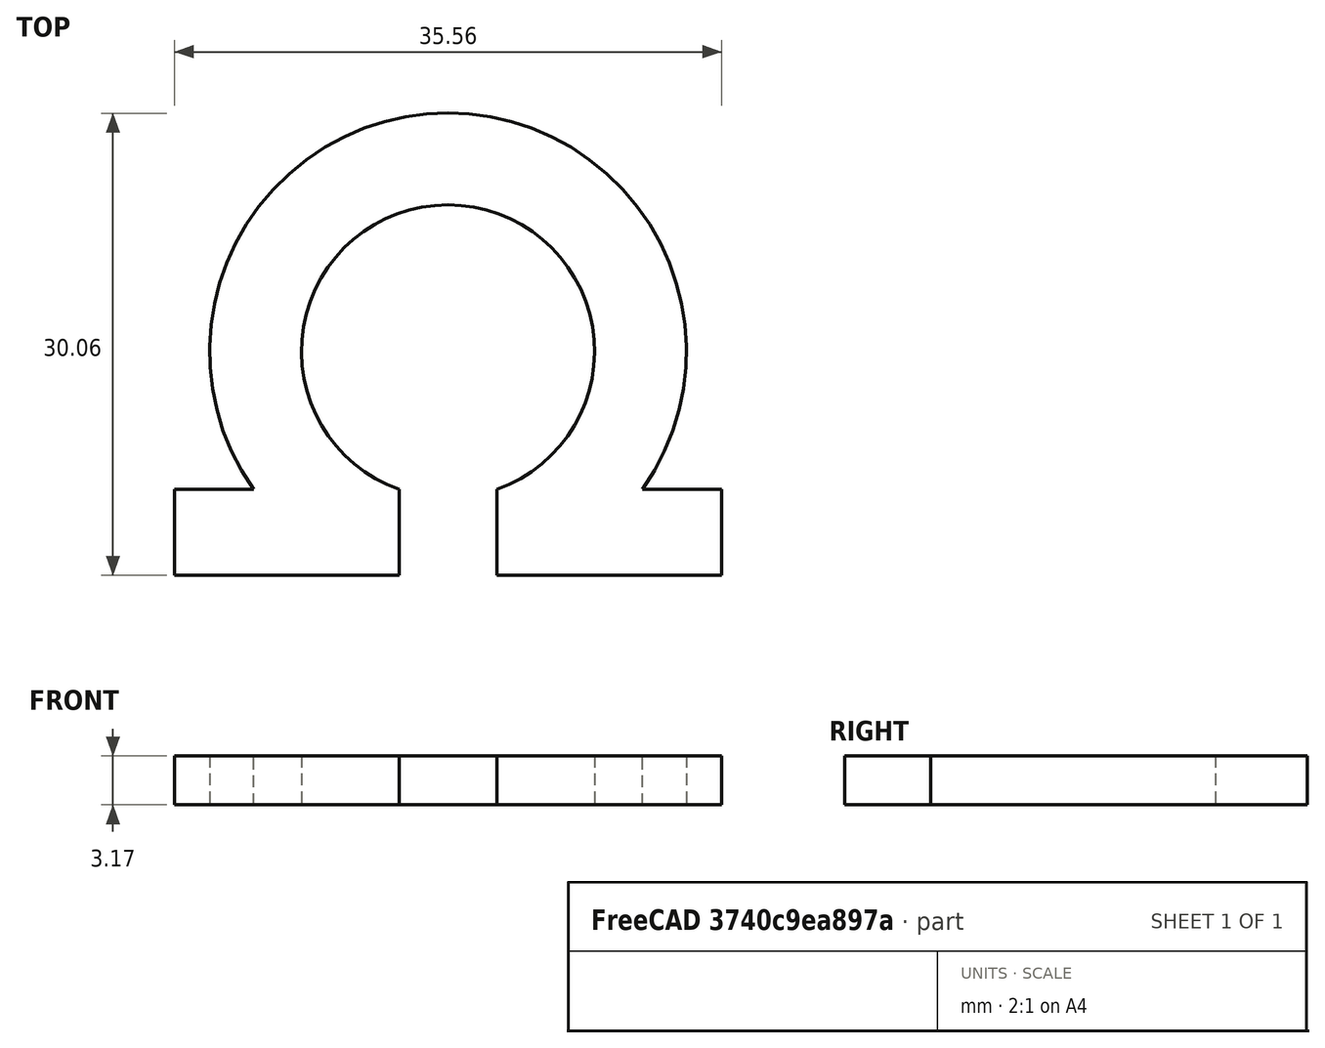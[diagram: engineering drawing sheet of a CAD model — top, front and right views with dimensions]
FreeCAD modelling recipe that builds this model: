
FCSTD DOCUMENT  (FreeCAD 0.20R26651 (Git))
Label: Electrical_Template
License: All rights reserved
LicenseURL: http://en.wikipedia.org/wiki/All_rights_reserved
objects: TechDraw::DrawViewDimension×7, Sketcher::SketchObject×1, PartDesign::Pad×1, PartDesign::Body×1, TechDraw::DrawSVGTemplate×1, TechDraw::DrawProjGroupItem×1, TechDraw::DrawProjGroup×1, TechDraw::DrawViewDimExtent×1, TechDraw::DrawPage×1
note: 4 computed .brp shape members not serialized (recipe doc carries the construction recipe); baked Part::Feature solids carry a one-line shape summary decoded from their .brp

FEATURE [Sketcher::SketchObject] Sketch
  FullyConstrained = true
  MapMode = 5
  Support = -> [XY_Plane]
  sketch-geometry (11):
    g0: LineSegment StartX=-17.78 StartY=-8.98026 StartZ=0 EndX=-17.78 EndY=-14.5683 EndZ=0
    g1: LineSegment StartX=-17.78 StartY=-14.5683 StartZ=0 EndX=-3.175 EndY=-14.5683 EndZ=0
    g2: LineSegment StartX=-3.175 StartY=-14.5683 StartZ=0 EndX=-3.175 EndY=-8.98026 EndZ=0
    g3: LineSegment StartX=-17.78 StartY=-8.98026 StartZ=0 EndX=-12.6261 EndY=-8.98026 EndZ=0
    g4: LineSegment StartX=3.175 StartY=-8.98026 StartZ=0 EndX=3.175 EndY=-14.5683 EndZ=0
    g5: LineSegment StartX=3.175 StartY=-14.5683 StartZ=0 EndX=17.78 EndY=-14.5683 EndZ=0
    g6: LineSegment StartX=17.78 StartY=-14.5683 StartZ=0 EndX=17.78 EndY=-8.98026 EndZ=0
    g7: LineSegment StartX=17.78 StartY=-8.98026 StartZ=0 EndX=12.6261 EndY=-8.98026 EndZ=0
    g8: ArcOfCircle CenterX=0 CenterY=0 CenterZ=0 NormalX=0 NormalY=0 NormalZ=1 AngleXU=0 Radius=15.494 StartAngle=5.66495 EndAngle=10.043
    g9: ArcOfCircle CenterX=0 CenterY=0 CenterZ=0 NormalX=0 NormalY=0 NormalZ=1 AngleXU=0 Radius=9.525 StartAngle=5.05223 EndAngle=10.6557
    g10: LineSegment StartX=12.6261 StartY=-8.98026 StartZ=0 EndX=-12.6261 EndY=-8.98026 EndZ=0
  constraints (31):
    c: Vertical(g0)
    c: Coincident(g1,g0)
    c: Horizontal(g1)
    c: Coincident(g2,g1)
    c: Vertical(g2)
    c: Coincident(g3,g0)
    c: Horizontal(g3)
    c: Vertical(g4)
    c: Coincident(g5,g4)
    c: Coincident(g6,g5)
    c: Vertical(g6)
    c: Coincident(g7,g6)
    c: Horizontal(g7)
    c: Coincident(g8,g-1)
    c: Coincident(g8,g7)
    c: Coincident(g8,g3)
    c: Coincident(g9,g8)
    c: Coincident(g9,g4)
    c: Coincident(g9,g2)
    c: Equal(g7,g3)
    c: Tangent(g1,g5)
    c: Equal(g1,g5)
    c: Equal(g4,g2)
    c: Distance(g0,g5) = 35.56
    c: Distance(g1,g4) = 6.35
    c: Distance(g0) = 5.588
    c: Diameter(g8) = 30.988
    c: Diameter(g9) = 19.05
    c: Coincident(g10,g7)
    c: Coincident(g10,g3)
    c: PointOnObject(g2,g10)
FEATURE [PartDesign::Pad] Pad
  Direction = (0,0,1)
  Length = 3.175
  Length2 = 100.076
  Profile = -> Sketch
  ReferenceAxis = -> Sketch [N_Axis]
  Type = 0
FEATURE [PartDesign::Body] Body  label="Ohmega Body"
  Group = -> [Sketch,Pad]
  Origin = -> Origin
  Tip = -> Pad
FEATURE [TechDraw::DrawSVGTemplate] Template
  EditableTexts = Designed_by_Name=Design by Matthew; Drawing_number=a94b4d95; FC-Date=Dec 2021; FC-SC=1:1; FC-SH=1 of 1; FC-Title=Electrical Subteam Patch; Subtitle=Tidal Force Robotics; Weight=0.01
  Height = 210
  Orientation = 1
  Width = 297
FEATURE [TechDraw::DrawProjGroupItem] ProjItem  label="Front"
  CoarseView = false
  Direction = (0,0,1)
  Focus = 100
  HardHidden = false
  IsoCount = 0
  IsoHidden = false
  IsoVisible = false
  LockPosition = true
  Perspective = false
  Rotation = 0
  RotationVector = (1,0,0)
  ScaleType = 2
  SeamHidden = false
  SeamVisible = true
  SmoothHidden = false
  SmoothVisible = true
  Source = -> [Body]
  Type = 0
  X = 0
  XDirection = (1,0,0)
  Y = 0
FEATURE [TechDraw::DrawProjGroup] ProjGroup
  Anchor = -> ProjItem
  AutoDistribute = true
  LockPosition = false
  ProjectionType = 0
  Rotation = 0
  ScaleType = 0
  Source = -> [Body]
  Views = -> [ProjItem]
  X = 143.364
  Y = 109.28
  spacingX = 14.986
  spacingY = 14.986
FEATURE [TechDraw::DrawViewDimension] Dimension
  Arbitrary = false
  ArbitraryTolerances = false
  EqualTolerance = true
  FormatSpec = %.3f
  FormatSpecOverTolerance = %+.3f
  FormatSpecUnderTolerance = %+.3f
  Inverted = false
  LockPosition = false
  MeasureType = 1
  OverTolerance = 0
  References2D = -> [ProjItem]
  Rotation = 0
  ScaleType = 0
  TheoreticalExact = false
  Type = 1
  UnderTolerance = 0
  X = 12.4986
  Y = -37.1923
FEATURE [TechDraw::DrawViewDimension] Dimension001
  Arbitrary = false
  ArbitraryTolerances = false
  EqualTolerance = true
  FormatSpec = %.3f
  FormatSpecOverTolerance = %+.3f
  FormatSpecUnderTolerance = %+.3f
  Inverted = false
  LockPosition = false
  MeasureType = 1
  OverTolerance = 0
  References2D = -> [ProjItem]
  Rotation = 0
  ScaleType = 0
  TheoreticalExact = false
  Type = 2
  UnderTolerance = 0
  X = 23.972
  Y = -20.0344
FEATURE [TechDraw::DrawViewDimension] Dimension002
  Arbitrary = false
  ArbitraryTolerances = false
  EqualTolerance = true
  FormatSpec = %.3f
  FormatSpecOverTolerance = %+.3f
  FormatSpecUnderTolerance = %+.3f
  Inverted = false
  LockPosition = false
  MeasureType = 1
  OverTolerance = 0
  References2D = -> [ProjItem]
  Rotation = 0
  ScaleType = 0
  TheoreticalExact = false
  Type = 1
  UnderTolerance = 0
  X = 11.008
  Y = -31.5737
FEATURE [TechDraw::DrawViewDimension] Dimension003
  Arbitrary = false
  ArbitraryTolerances = false
  EqualTolerance = true
  FormatSpec = ⌀%.3f
  FormatSpecOverTolerance = %+.3f
  FormatSpecUnderTolerance = %+.3f
  Inverted = false
  LockPosition = false
  MeasureType = 1
  OverTolerance = 0
  References2D = -> [ProjItem]
  Rotation = 0
  ScaleType = 0
  TheoreticalExact = false
  Type = 5
  UnderTolerance = 0
  X = -27.6345
  Y = 9.17329
FEATURE [TechDraw::DrawViewDimension] Dimension004
  Arbitrary = false
  ArbitraryTolerances = false
  EqualTolerance = true
  FormatSpec = ⌀%.3f
  FormatSpecOverTolerance = %+.3f
  FormatSpecUnderTolerance = %+.3f
  Inverted = false
  LockPosition = false
  MeasureType = 1
  OverTolerance = 0
  References2D = -> [ProjItem]
  Rotation = 0
  ScaleType = 0
  TheoreticalExact = false
  Type = 5
  UnderTolerance = 0
  X = -26.3732
  Y = 15.0213
FEATURE [TechDraw::DrawViewDimExtent] DimExtent
  Arbitrary = false
  ArbitraryTolerances = false
  CosmeticTags = 0f7ad2d1-9a02-4d76-9d73-bacf5d1081f6 | a075bab9-b7a2-4d22-8606-70dbb64c4bad
  DirExtent = 1
  EqualTolerance = true
  FormatSpec = %.3f
  FormatSpecOverTolerance = %+.3f
  FormatSpecUnderTolerance = %+.3f
  Inverted = false
  LockPosition = false
  MeasureType = 1
  OverTolerance = 0
  References2D = -> [ProjItem]
  Rotation = 0
  ScaleType = 0
  Source = -> [ProjItem]
  TheoreticalExact = false
  Type = 2
  UnderTolerance = 0
  X = 45.4078
  Y = 1.03199
FEATURE [TechDraw::DrawViewDimension] Dimension005
  Arbitrary = false
  ArbitraryTolerances = false
  EqualTolerance = true
  FormatSpec = %.3f
  FormatSpecOverTolerance = %+.3f
  FormatSpecUnderTolerance = %+.3f
  Inverted = false
  LockPosition = false
  MeasureType = 1
  OverTolerance = 0
  References2D = -> [ProjItem]
  Rotation = 0
  ScaleType = 0
  TheoreticalExact = false
  Type = 2
  UnderTolerance = 0
  X = -29.222
  Y = -6.14167
FEATURE [TechDraw::DrawViewDimension] Dimension006
  Arbitrary = false
  ArbitraryTolerances = false
  EqualTolerance = true
  FormatSpec = %.3f
  FormatSpecOverTolerance = %+.3f
  FormatSpecUnderTolerance = %+.3f
  Inverted = false
  LockPosition = false
  MeasureType = 1
  OverTolerance = 0
  References2D = -> [ProjItem]
  Rotation = 0
  ScaleType = 0
  TheoreticalExact = false
  Type = 1
  UnderTolerance = 0
  X = -8.89
  Y = 24.1722
FEATURE [TechDraw::DrawPage] Page
  KeepUpdated = true
  NextBalloonIndex = 1
  ProjectionType = 0
  Template = -> Template
  Views = -> [ProjGroup,Dimension,Dimension001,Dimension002,Dimension003,Dimension004,DimExtent,Dimension005,Dimension006]
